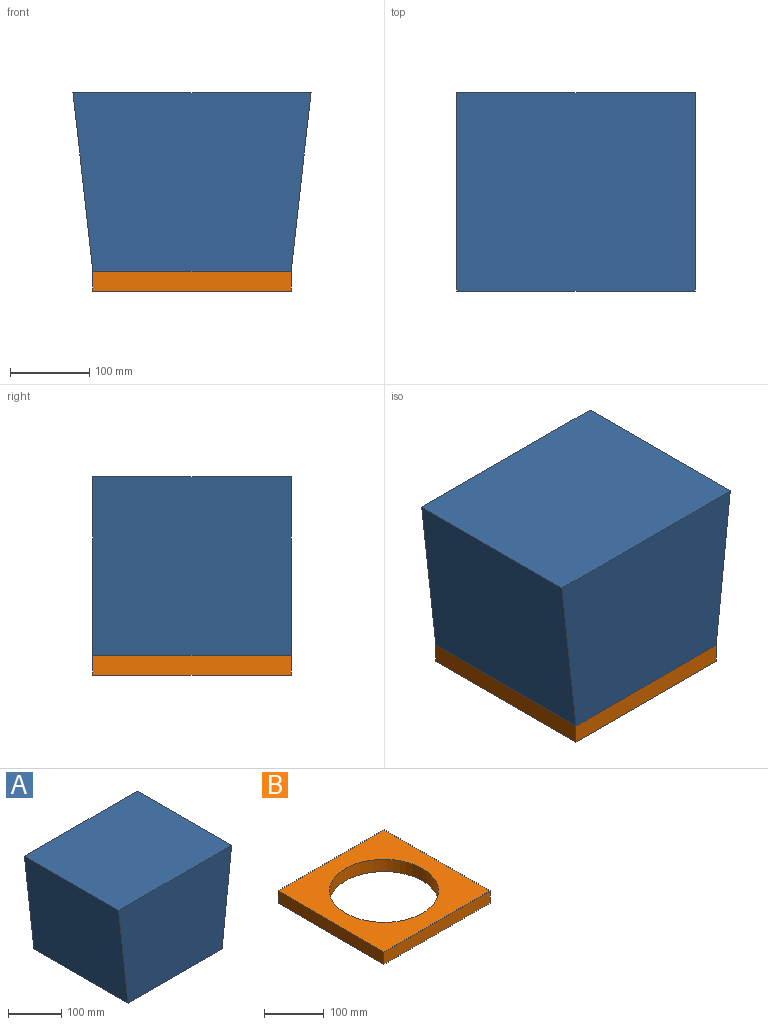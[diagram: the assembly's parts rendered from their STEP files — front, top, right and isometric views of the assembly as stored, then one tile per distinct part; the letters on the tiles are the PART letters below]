
ASSEMBLY  parts=2 mates=1
PART A: 6 faces, bbox 300x250x225 mm
  f0: plane 300x250mm, normal (0,0,1), area 75000mm2, adj f1,f3,f4,f5
  f1: plane 250x225mm, normal (-0.99,0,-0.11), area 56596.2mm2, adj f0,f2,f4,f5
  f2: plane 250x250mm, normal (0,0,-1), area 62500mm2, adj f1,f3,f4,f5
  f3: plane 250x225mm, normal (0.99,0,-0.11), area 56596.2mm2, adj f0,f2,f4,f5
  f4: plane 300x225mm, normal (0,1,0), area 61875mm2, adj f0,f1,f2,f3
  f5: plane 300x225mm, normal (0,-1,0), area 61875mm2, adj f0,f1,f2,f3
PART B: 7 faces, bbox 250x250x25 mm
  f0: plane 250x25mm, normal (1,0,0), area 6250mm2, adj f1,f4,f5,f6
  f1: plane 250x25mm, normal (0,1,0), area 6250mm2, adj f0,f2,f5,f6
  f2: plane 250x25mm, normal (-1,0,0), area 6250mm2, adj f1,f4,f5,f6
  f3: cylinder r=91mm len=182mm, axis (0,0,1), area 14294.2mm2, adj f5,f6
  f4: plane 250x25mm, normal (0,-1,0), area 6250mm2, adj f0,f2,f5,f6
  f5: plane 250x250mm, normal (0,0,-1), area 36484.5mm2, adj f0,f1,f2,f3,f4
  f6: plane 250x250mm, normal (0,0,1), area 36484.5mm2, adj f0,f1,f2,f3,f4
PLACE A t=(-6.83,-145.98,99.44)mm
PLACE B t=(-6.83,-20.98,-13.06)mm
MATE fastened A.f2 <-> B.f3  axis (0,0,-1) through (-6.83,-20.98,-13.06)mm
